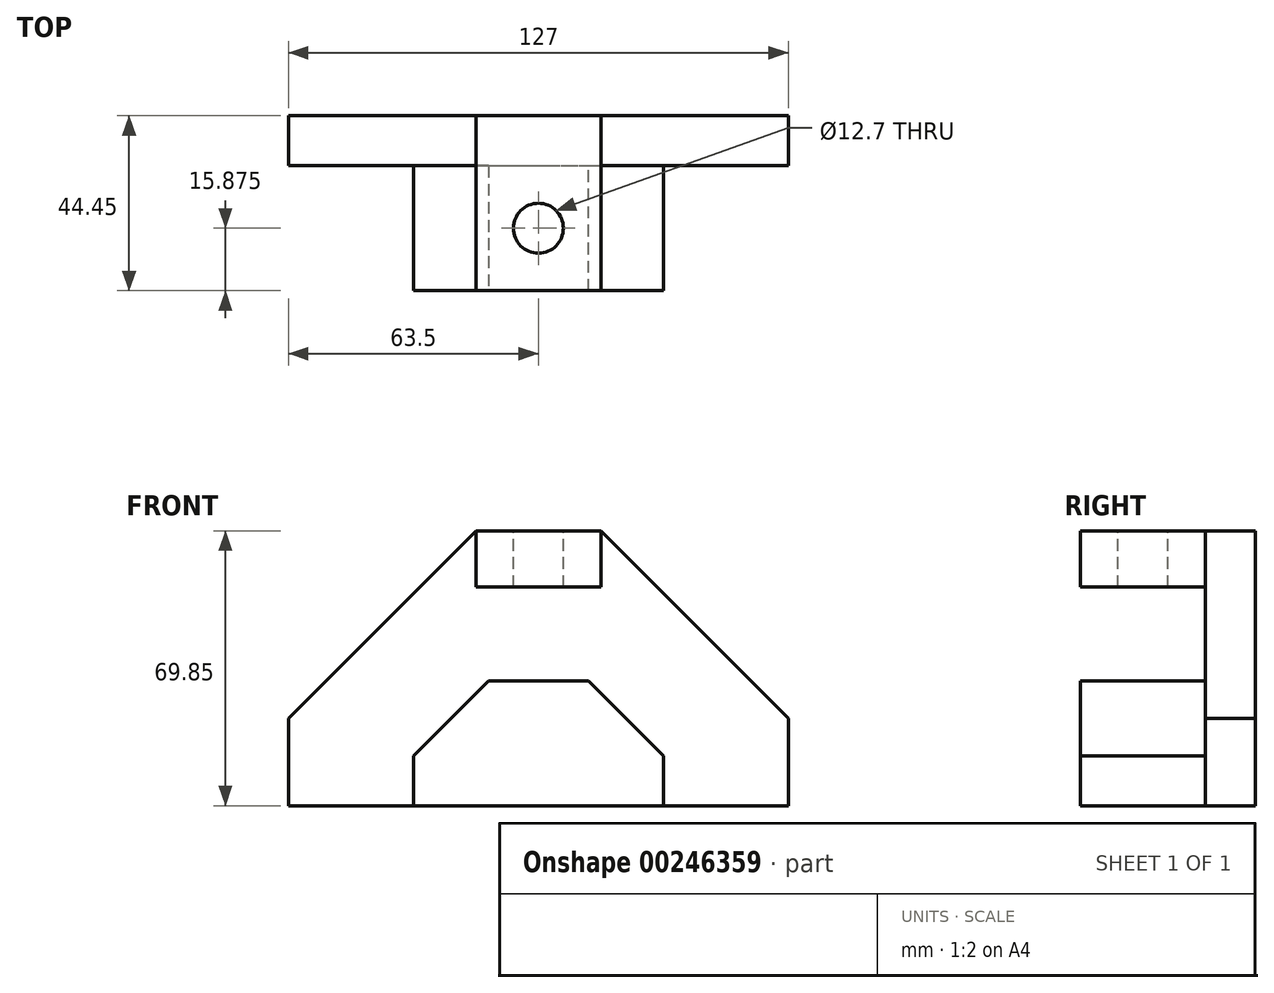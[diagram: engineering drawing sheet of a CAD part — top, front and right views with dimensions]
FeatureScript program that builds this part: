
annotation { "Feature Type Name" : "Feature", "Feature Type Description" : "" }
export const myFeature = defineFeature(function(context is Context, id is Id, definition is map)
    precondition{}
    {
        {
            var Q0;
            Q0=qCreatedBy(makeId("Front.planeOp"),FACE);
            var sketch = newSketch(context, id + "F0", { "sketchPlane" : qUnion([Q0])});
            skLineSegment(sketch, "E0.bottom", {"start": v(0, 69.85) * mm, "end": v(127, 69.85) * mm});
            skLineSegment(sketch, "E0.top", {"start": v(0, 0) * mm, "end": v(127, 0) * mm});
            skLineSegment(sketch, "E0.left", {"start": v(0, 69.85) * mm, "end": v(0, 0) * mm});
            skLineSegment(sketch, "E0.right", {"start": v(127, 69.85) * mm, "end": v(127, 0) * mm});
            skSolve(sketch);
        }
        {
            var Q0;
            Q0 = qSketchRegion(id + "F0", true);
            extrude(context, id + "F1", {"entities" : qUnion([Q0]), "depth" : 12.7 * mm});
        }
        {
            var Q0;
            Q0=makeQuery(id+"F1.opExtrude","SWEPT_EDGE",EDGE,{"disambiguationData":[OSD([sQuery(id+"F0.wireOp",EDGE,"E0.bottom"),sQuery(id+"F0.wireOp",EDGE,"E0.left")])]});
            var Q1;
            Q1=makeQuery(id+"F1.opExtrude","SWEPT_EDGE",EDGE,{"disambiguationData":[OSD([sQuery(id+"F0.wireOp",EDGE,"E0.bottom"),sQuery(id+"F0.wireOp",EDGE,"E0.right")])]});
            chamfer(context, id + "F2", {"entities" : qUnion([Q0, Q1]), "width" : 47.62 * mm, "tangentPropagation" : true});
        }
        {
            var Q0;
            Q0=makeQuery(id+"F1.opExtrude","CAP_FACE",FACE,{"disambiguationData":[OSD([sQuery(id+"F0.wireOp",EDGE,"E0.bottom"),sQuery(id+"F0.wireOp",EDGE,"E0.top"),sQuery(id+"F0.wireOp",EDGE,"E0.left"),sQuery(id+"F0.wireOp",EDGE,"E0.right")])],"isStart":false});
            var sketch = newSketch(context, id + "F3", { "sketchPlane" : qUnion([Q0])});
            skLineSegment(sketch, "E1.bottom", {"start": v(47.63, 69.85) * mm, "end": v(79.38, 69.85) * mm});
            skLineSegment(sketch, "E1.top", {"start": v(47.63, 55.56) * mm, "end": v(79.38, 55.56) * mm});
            skLineSegment(sketch, "E1.left", {"start": v(47.63, 69.85) * mm, "end": v(47.63, 55.56) * mm});
            skLineSegment(sketch, "E1.right", {"start": v(79.38, 69.85) * mm, "end": v(79.38, 55.56) * mm});
            skLineSegment(sketch, "E2.bottom", {"start": v(31.75, 0) * mm, "end": v(95.25, 0) * mm});
            skLineSegment(sketch, "E2.top", {"start": v(31.75, 31.75) * mm, "end": v(95.25, 31.75) * mm});
            skLineSegment(sketch, "E2.left", {"start": v(31.75, 0) * mm, "end": v(31.75, 31.75) * mm});
            skLineSegment(sketch, "E2.right", {"start": v(95.25, 0) * mm, "end": v(95.25, 31.75) * mm});
            skSolve(sketch);
        }
        {
            var Q0;
            Q0=makeQuery(id+"F3.imprint","IMPRINT",FACE,{"disambiguationData":[TD([[makeQuery(id+"F3.imprint","IMPRINT",EDGE,{"derivedFrom":sQuery(id+"F3.wireOp",EDGE,"E1.bottom")}),-1.0]])]});
            var Q1;
            Q1=makeQuery(id+"F3.imprint","IMPRINT",FACE,{"disambiguationData":[TD([[makeQuery(id+"F3.imprint","IMPRINT",EDGE,{"derivedFrom":sQuery(id+"F3.wireOp",EDGE,"E2.bottom")}),1.0]])]});
            extrude(context, id + "F4", {"entities" : qUnion([Q0, Q1]), "operationType" : NewBodyOperationType.ADD, "depth" : 31.75 * mm});
        }
        {
            var Q0;
            Q0=makeQuery(id+"F4.opExtrude","SWEPT_EDGE",EDGE,{"disambiguationData":[OSD([sQuery(id+"F3.wireOp",EDGE,"E2.top"),sQuery(id+"F3.wireOp",EDGE,"E2.left")])]});
            var Q1;
            Q1=makeQuery(id+"F4.opExtrude","SWEPT_EDGE",EDGE,{"disambiguationData":[OSD([sQuery(id+"F3.wireOp",EDGE,"E2.top"),sQuery(id+"F3.wireOp",EDGE,"E2.right")])]});
            chamfer(context, id + "F5", {"entities" : qUnion([Q0, Q1]), "width" : 19.05 * mm, "tangentPropagation" : true});
        }
        {
            var Q0;
            Q0=makeQuery(id+"F4.boolean.opBoolean","MERGE",FACE,{"derivedFrom":[makeQuery(id+"F1.opExtrude","SWEPT_FACE",FACE,{"disambiguationData":[OSD([sQuery(id+"F0.wireOp",EDGE,"E0.bottom")])]}),makeQuery(id+"F4.opExtrude","SWEPT_FACE",FACE,{"disambiguationData":[OSD([sQuery(id+"F3.wireOp",EDGE,"E1.bottom")])]})]});
            var sketch = newSketch(context, id + "F6", { "sketchPlane" : qUnion([Q0])});
            skCircle(sketch, "E3", {"center": v(63.5, -28.58) * mm, "radius": 6.35 * mm});
            skPoint(sketch, "E3.centerSnap0", {"position": v(63.5, -44.45) * mm});
            skSolve(sketch);
        }
        {
            var Q0;
            Q0=makeQuery(id+"F6.imprint","IMPRINT",FACE,{"disambiguationData":[TD([[makeQuery(id+"F6.imprint","IMPRINT",EDGE,{"derivedFrom":sQuery(id+"F6.wireOp",EDGE,"E3")}),1.0]])]});
            extrude(context, id + "F7", {"entities" : qUnion([Q0]), "operationType" : NewBodyOperationType.REMOVE, "oppositeDirection" : true, "depth" : 14.29 * mm});
        }
    });
